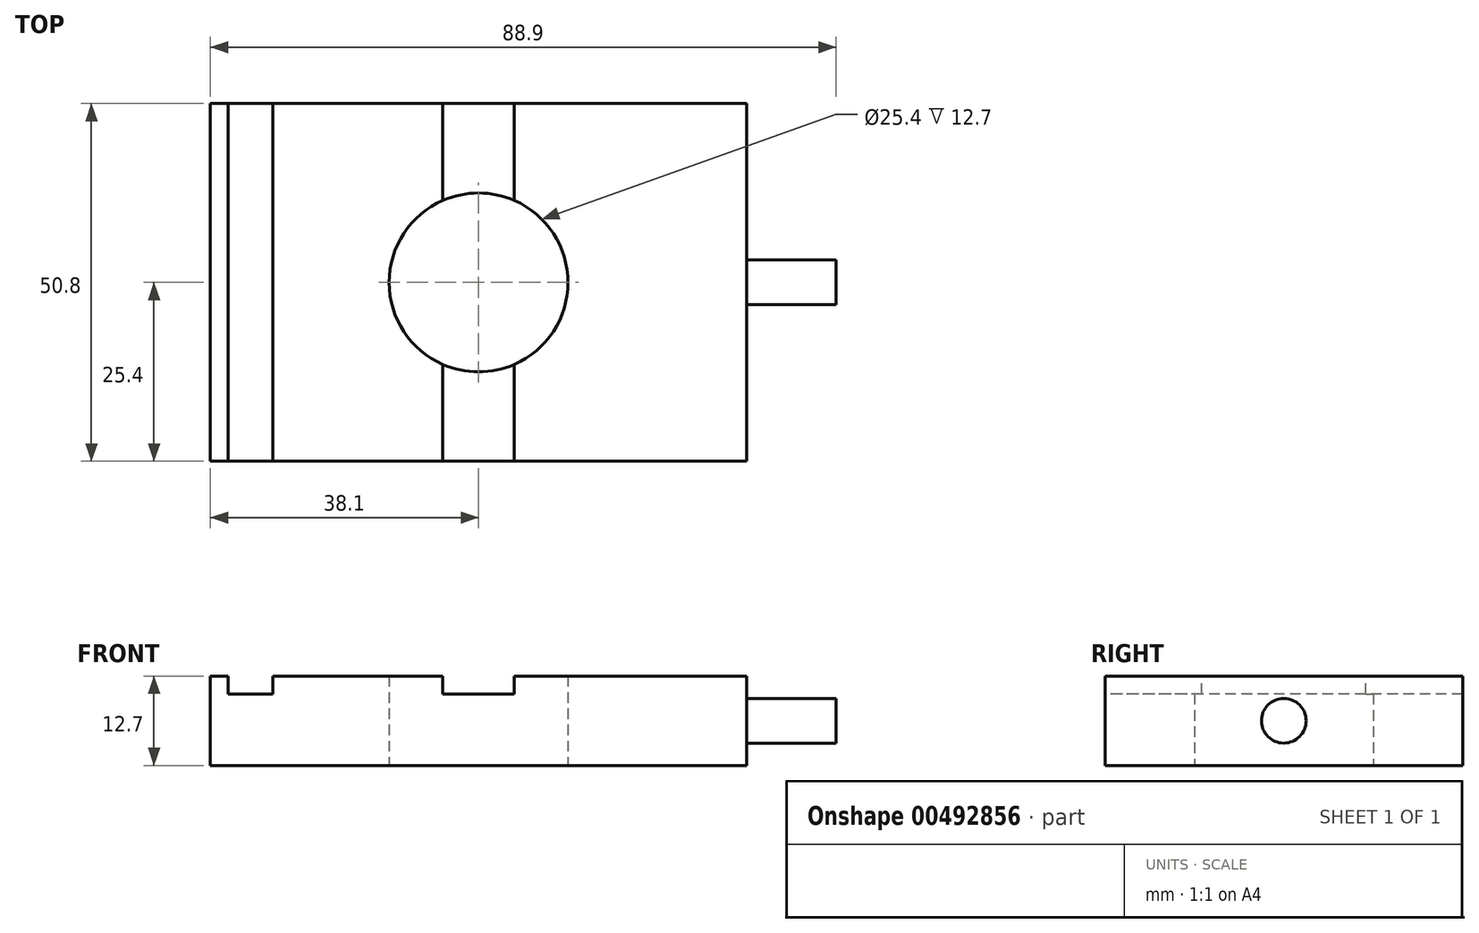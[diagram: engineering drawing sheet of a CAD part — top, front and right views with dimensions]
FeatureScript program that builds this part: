
annotation { "Feature Type Name" : "Feature", "Feature Type Description" : "" }
export const myFeature = defineFeature(function(context is Context, id is Id, definition is map)
    precondition{}
    {
        {
            var Q0;
            Q0=qCreatedBy(makeId("Top.planeOp"),FACE);
            var sketch = newSketch(context, id + "F0", { "sketchPlane" : qUnion([Q0])});
            skLineSegment(sketch, "E0.bottom", {"start": v(38.1, -25.4) * mm, "end": v(-38.1, -25.4) * mm});
            skLineSegment(sketch, "E0.top", {"start": v(38.1, 25.4) * mm, "end": v(-38.1, 25.4) * mm});
            skLineSegment(sketch, "E0.left", {"start": v(38.1, -25.4) * mm, "end": v(38.1, 25.4) * mm});
            skLineSegment(sketch, "E0.right", {"start": v(-38.1, -25.4) * mm, "end": v(-38.1, 25.4) * mm});
            skPoint(sketch, "E0.middle", {"position": v(0, 0) * mm});
            skCircle(sketch, "E1", {"center": v(0, 0) * mm, "radius": 12.7 * mm});
            skSolve(sketch);
        }
        {
            var Q0;
            Q0 = qSketchRegion(id + "F0", true);
            extrude(context, id + "F1", {"entities" : qUnion([Q0]), "depth" : 12.7 * mm, "offsetDistance" : 25.4 * mm});
        }
        {
            var Q0;
            Q0=makeQuery(id+"F1.opExtrude","CAP_FACE",FACE,{"disambiguationData":[OSD([sQuery(id+"F0.wireOp",EDGE,"E0.bottom"),sQuery(id+"F0.wireOp",EDGE,"E0.top"),sQuery(id+"F0.wireOp",EDGE,"E0.left"),sQuery(id+"F0.wireOp",EDGE,"E0.right"),sQuery(id+"F0.wireOp",EDGE,"E1")])],"isStart":false});
            var sketch = newSketch(context, id + "F2", { "sketchPlane" : qUnion([Q0])});
            skLineSegment(sketch, "E2.bottom", {"start": v(-35.56, 25.4) * mm, "end": v(-29.21, 25.4) * mm});
            skLineSegment(sketch, "E2.top", {"start": v(-35.56, -25.4) * mm, "end": v(-29.21, -25.4) * mm});
            skLineSegment(sketch, "E2.left", {"start": v(-35.56, 25.4) * mm, "end": v(-35.56, -25.4) * mm});
            skLineSegment(sketch, "E2.right", {"start": v(-29.21, 25.4) * mm, "end": v(-29.21, -25.4) * mm});
            skLineSegment(sketch, "E3.bottom", {"start": v(-5.08, 25.4) * mm, "end": v(5.08, 25.4) * mm});
            skLineSegment(sketch, "E3.top", {"start": v(-5.08, -25.4) * mm, "end": v(5.08, -25.4) * mm});
            skLineSegment(sketch, "E3.left", {"start": v(-5.08, 25.4) * mm, "end": v(-5.08, -25.4) * mm});
            skLineSegment(sketch, "E3.right", {"start": v(5.08, 25.4) * mm, "end": v(5.08, -25.4) * mm});
            skLineSegment(sketch, "E4", {"start": v(0, 0) * mm, "end": v(0, 25.4) * mm, "construction": true});
            skLineSegment(sketch, "E5", {"start": v(0, 25.4) * mm, "end": v(0, -25.4) * mm, "construction": true});
            skSolve(sketch);
        }
        {
            var Q0;
            Q0=makeQuery(id+"F2.imprint","IMPRINT",FACE,{"disambiguationData":[TD([[makeQuery(id+"F2.imprint","IMPRINT",EDGE,{"derivedFrom":sQuery(id+"F2.wireOp",EDGE,"E2.bottom")}),1.0]])]});
            var Q1;
            {var subQ0=sQuery(id+"F2.wireOp",EDGE,"E3.bottom");Q1=makeQuery(id+"F2.imprint","IMPRINT",FACE,{"disambiguationData":[TD([[makeQuery(id+"F2.imprint","IMPRINT",EDGE,{"derivedFrom":subQ0}),1.0]])]});}
            var Q2;
            {var subQ0=sQuery(id+"F2.wireOp",EDGE,"E3.top");Q2=makeQuery(id+"F2.imprint","IMPRINT",FACE,{"disambiguationData":[TD([[makeQuery(id+"F2.imprint","IMPRINT",EDGE,{"derivedFrom":subQ0}),-1.0]])]});}
            extrude(context, id + "F3", {"entities" : qUnion([Q0, Q1, Q2]), "operationType" : NewBodyOperationType.REMOVE, "oppositeDirection" : true, "depth" : 2.54 * mm, "offsetDistance" : 25.4 * mm});
        }
        {
            var Q0;
            Q0=makeQuery(id+"F1.opExtrude","SWEPT_FACE",FACE,{"disambiguationData":[OSD([sQuery(id+"F0.wireOp",EDGE,"E0.left")])]});
            var sketch = newSketch(context, id + "F4", { "sketchPlane" : qUnion([Q0])});
            skLineSegment(sketch, "E6", {"start": v(0, 0) * mm, "end": v(0, 12.7) * mm, "construction": true});
            skLineSegment(sketch, "E7", {"start": v(-25.4, 6.35) * mm, "end": v(25.4, 6.35) * mm, "construction": true});
            skCircle(sketch, "E8", {"center": v(0, 6.35) * mm, "radius": 3.18 * mm});
            skSolve(sketch);
        }
        {
            var Q0;
            Q0 = qSketchRegion(id + "F4", true);
            extrude(context, id + "F5", {"entities" : qUnion([Q0]), "operationType" : NewBodyOperationType.ADD, "depth" : 12.7 * mm, "offsetDistance" : 25.4 * mm});
        }
    });
